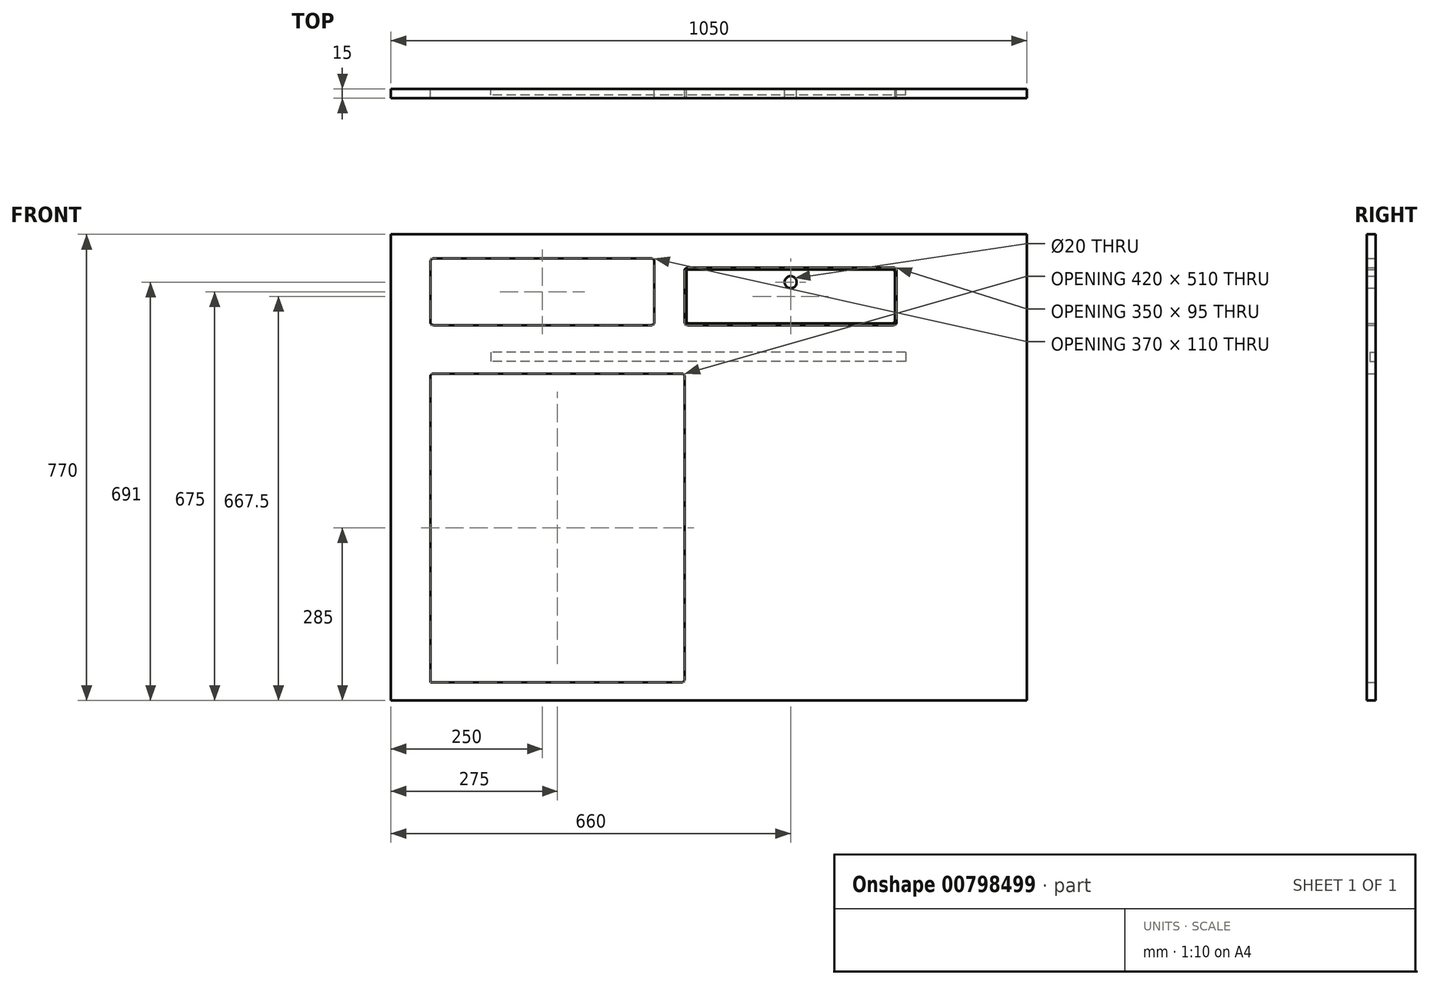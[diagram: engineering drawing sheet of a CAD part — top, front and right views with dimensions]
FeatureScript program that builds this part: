
annotation { "Feature Type Name" : "Feature", "Feature Type Description" : "" }
export const myFeature = defineFeature(function(context is Context, id is Id, definition is map)
    precondition{}
    {
        {
            var Q0;
            Q0=qCreatedBy(makeId("Front.planeOp"),FACE);
            var sketch = newSketch(context, id + "F0", { "sketchPlane" : qUnion([Q0])});
            skLineSegment(sketch, "E0.bottom", {"start": v(0, 0) * mm, "end": v(1050, 0) * mm});
            skLineSegment(sketch, "E0.top", {"start": v(0, -770) * mm, "end": v(1050, -770) * mm});
            skLineSegment(sketch, "E0.left", {"start": v(0, 0) * mm, "end": v(0, -770) * mm});
            skLineSegment(sketch, "E0.right", {"start": v(1050, 0) * mm, "end": v(1050, -770) * mm});
            skLineSegment(sketch, "E1.bottom", {"start": v(65, -740) * mm, "end": v(480, -740) * mm});
            skLineSegment(sketch, "E1.top", {"start": v(70, -230) * mm, "end": v(480, -230) * mm});
            skLineSegment(sketch, "E1.left", {"start": v(65, -740) * mm, "end": v(65, -235) * mm});
            skLineSegment(sketch, "E1.right", {"start": v(485, -735) * mm, "end": v(485, -235) * mm});
            skLineSegment(sketch, "E2.bottom", {"start": v(70, -40) * mm, "end": v(430, -40) * mm});
            skLineSegment(sketch, "E2.top", {"start": v(70, -150) * mm, "end": v(430, -150) * mm});
            skLineSegment(sketch, "E2.left", {"start": v(65, -45) * mm, "end": v(65, -145) * mm});
            skLineSegment(sketch, "E2.right", {"start": v(435, -45) * mm, "end": v(435, -145) * mm});
            skLineSegment(sketch, "E3.bottom", {"start": v(490, -150) * mm, "end": v(830, -150) * mm});
            skLineSegment(sketch, "E3.top", {"start": v(490, -55) * mm, "end": v(830, -55) * mm});
            skLineSegment(sketch, "E3.left", {"start": v(485, -145) * mm, "end": v(485, -60) * mm});
            skLineSegment(sketch, "E3.right", {"start": v(835, -145) * mm, "end": v(835, -60) * mm});
            skPoint(sketch, "E4.visualSharp", {"position": v(65, -40) * mm});
            skArc(sketch, "E4.filletArc", {"start": v(70, -40) * mm, "mid": v(66.46, -41.46) * mm, "end": v(65, -45) * mm});
            skPoint(sketch, "E5.visualSharp", {"position": v(65, -150) * mm});
            skArc(sketch, "E5.filletArc", {"start": v(65, -145) * mm, "mid": v(66.46, -148.54) * mm, "end": v(70, -150) * mm});
            skPoint(sketch, "E6.visualSharp", {"position": v(435, -150) * mm});
            skArc(sketch, "E6.filletArc", {"start": v(430, -150) * mm, "mid": v(433.54, -148.54) * mm, "end": v(435, -145) * mm});
            skPoint(sketch, "E7.visualSharp", {"position": v(435, -40) * mm});
            skArc(sketch, "E7.filletArc", {"start": v(435, -45) * mm, "mid": v(433.54, -41.46) * mm, "end": v(430, -40) * mm});
            skPoint(sketch, "E8.visualSharp", {"position": v(485, -55) * mm});
            skArc(sketch, "E8.filletArc", {"start": v(490, -55) * mm, "mid": v(486.46, -56.46) * mm, "end": v(485, -60) * mm});
            skPoint(sketch, "E9.visualSharp", {"position": v(485, -150) * mm});
            skArc(sketch, "E9.filletArc", {"start": v(485, -145) * mm, "mid": v(486.46, -148.54) * mm, "end": v(490, -150) * mm});
            skPoint(sketch, "E10.visualSharp", {"position": v(835, -150) * mm});
            skArc(sketch, "E10.filletArc", {"start": v(830, -150) * mm, "mid": v(833.54, -148.54) * mm, "end": v(835, -145) * mm});
            skPoint(sketch, "E11.visualSharp", {"position": v(835, -55) * mm});
            skArc(sketch, "E11.filletArc", {"start": v(835, -60) * mm, "mid": v(833.54, -56.46) * mm, "end": v(830, -55) * mm});
            skPoint(sketch, "E12.visualSharp", {"position": v(65, -230) * mm});
            skArc(sketch, "E12.filletArc", {"start": v(70, -230) * mm, "mid": v(66.46, -231.46) * mm, "end": v(65, -235) * mm});
            skPoint(sketch, "E13.visualSharp", {"position": v(485, -230) * mm});
            skArc(sketch, "E13.filletArc", {"start": v(485, -235) * mm, "mid": v(483.54, -231.46) * mm, "end": v(480, -230) * mm});
            skPoint(sketch, "E14.visualSharp", {"position": v(485, -740) * mm});
            skArc(sketch, "E14.filletArc", {"start": v(480, -740) * mm, "mid": v(483.54, -738.54) * mm, "end": v(485, -735) * mm});
            skLineSegment(sketch, "E15.0", {"start": v(492, -147) * mm, "end": v(828, -147) * mm});
            skLineSegment(sketch, "E15.1", {"start": v(488, -143) * mm, "end": v(488, -62) * mm});
            skLineSegment(sketch, "E15.2", {"start": v(492, -58) * mm, "end": v(828, -58) * mm});
            skLineSegment(sketch, "E15.3", {"start": v(832, -143) * mm, "end": v(832, -62) * mm});
            skPoint(sketch, "E16.visualSharp", {"position": v(488, -58) * mm});
            skArc(sketch, "E16.filletArc", {"start": v(492, -58) * mm, "mid": v(489.17, -59.17) * mm, "end": v(488, -62) * mm});
            skPoint(sketch, "E17.visualSharp", {"position": v(488, -147) * mm});
            skArc(sketch, "E17.filletArc", {"start": v(488, -143) * mm, "mid": v(489.17, -145.83) * mm, "end": v(492, -147) * mm});
            skPoint(sketch, "E18.visualSharp", {"position": v(832, -147) * mm});
            skArc(sketch, "E18.filletArc", {"start": v(828, -147) * mm, "mid": v(830.83, -145.83) * mm, "end": v(832, -143) * mm});
            skPoint(sketch, "E19.visualSharp", {"position": v(832, -58) * mm});
            skArc(sketch, "E19.filletArc", {"start": v(832, -62) * mm, "mid": v(830.83, -59.17) * mm, "end": v(828, -58) * mm});
            skCircle(sketch, "E20", {"center": v(660, -79) * mm, "radius": 10 * mm});
            skLineSegment(sketch, "E21.bottom", {"start": v(850, -195) * mm, "end": v(165, -195) * mm});
            skLineSegment(sketch, "E21.top", {"start": v(850, -210) * mm, "end": v(165, -210) * mm});
            skLineSegment(sketch, "E21.left", {"start": v(850, -195) * mm, "end": v(850, -210) * mm});
            skLineSegment(sketch, "E21.right", {"start": v(165, -195) * mm, "end": v(165, -210) * mm});
            skSolve(sketch);
        }
        {
            var Q0;
            Q0=makeQuery(id+"F0.imprint","IMPRINT",FACE,{"disambiguationData":[TD([[makeQuery(id+"F0.imprint","IMPRINT",EDGE,{"derivedFrom":sQuery(id+"F0.wireOp",EDGE,"E15.0")}),1.0]])]});
            var Q1;
            Q1=makeQuery(id+"F0.imprint","IMPRINT",FACE,{"disambiguationData":[TD([[makeQuery(id+"F0.imprint","IMPRINT",EDGE,{"derivedFrom":sQuery(id+"F0.wireOp",EDGE,"E21.bottom")}),1.0]])]});
            var Q2;
            Q2=makeQuery(id+"F0.imprint","IMPRINT",FACE,{"disambiguationData":[TD([[makeQuery(id+"F0.imprint","IMPRINT",EDGE,{"derivedFrom":sQuery(id+"F0.wireOp",EDGE,"E0.bottom")}),-1.0]])]});
            extrude(context, id + "F1", {"entities" : qUnion([Q0, Q1, Q2]), "depth" : 15 * mm, "offsetDistance" : 25 * mm});
        }
        {
            var Q0;
            Q0=makeQuery(id+"F0.imprint","IMPRINT",FACE,{"disambiguationData":[TD([[makeQuery(id+"F0.imprint","IMPRINT",EDGE,{"derivedFrom":sQuery(id+"F0.wireOp",EDGE,"E21.bottom")}),1.0]])]});
            extrude(context, id + "F2", {"entities" : qUnion([Q0]), "operationType" : NewBodyOperationType.REMOVE, "depth" : 10 * mm, "offsetDistance" : 25 * mm});
        }
    });
